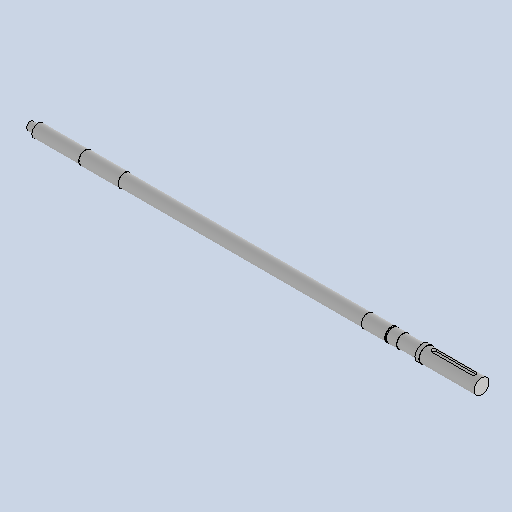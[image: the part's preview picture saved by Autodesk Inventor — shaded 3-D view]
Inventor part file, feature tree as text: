
AUTODESK INVENTOR PART (.ipt)
format: ipt  version: 2025 (Build 290162010, 162A)  size: 309,248 bytes
history: native  units: mm
features: sketch x2, revolve x1, plane x1, extrude x1, projected_geometry x1
ambient origin geometry x8: Origin, YZ Plane, XZ Plane, XY Plane, X Axis, Y Axis, Z Axis, Center Point
bodies: Solid1 (feature_tree)
feature tree (6):
  revolve  "Revolution1"  Angle=360.0deg
  plane  "Work Plane1"
  extrude  "Extrusion1"  Depth=10.0mm
  sketch  "Sketch1"  dims[d0=16.4mm d2=360.0deg]
  sketch  "Sketch2"  dims[d3=17.0mm d5=50.0mm d6=460.0mm d7=45.0mm d9=17.0mm d10=115.0mm d11=19.0mm d12=20.0mm d13=5.0mm d14=70.0mm d16=15.0mm d17=2.0mm d18=15.0mm d19=340.0mm d20=6.0mm d21=50.0mm d22=35.0mm d23=3.0mm d24=0.0mm d25=10.0mm d26=10.0mm]
  projected_geometry  "Projected Loop1"
